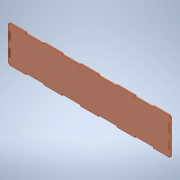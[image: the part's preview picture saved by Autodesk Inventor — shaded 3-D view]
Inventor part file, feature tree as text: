
AUTODESK INVENTOR PART (.ipt)
format: ipt  version: 2020.3 (Build 243373000, 373)  size: 240,128 bytes
history: native  units: mm
features: sketch x3, extrude x2, other x1
ambient origin geometry x8: Origin, YZ Plane, XZ Plane, XY Plane, X Axis, Y Axis, Z Axis, Center Point
bodies: Body1 (feature_tree)
feature tree (6):
  other  "Sólido1"
  extrude  "Extrusión1"  Depth=94.0mm
  sketch  "Boceto2"  dims[d2=3.0mm d3=3.0mm]
  extrude  "Extrusión2"  Depth=3.0mm
  sketch  "Boceto1"  dims[d0=3.0mm d1=94.0mm]
  sketch  "Boceto3"  dims[d4=45.0mm d5=3.0mm d6=50.0mm d7=3.0mm d8=50.0mm d9=3.0mm d10=50.0mm d11=3.0mm d12=50.0mm d13=3.0mm d14=50.0mm d15=3.0mm d16=50.0mm d17=3.0mm d18=50.0mm d19=3.0mm d20=45.0mm d21=3.0mm d22=3.0mm d23=94.0mm d41=3.0mm d42=45.0mm d43=3.0mm d44=50.0mm d45=3.0mm d46=50.0mm d58=3.0mm d59=50.0mm d60=3.0mm d61=50.0mm d62=3.0mm d63=50.0mm d64=3.0mm d65=50.0mm d66=3.0mm d67=50.0mm d68=3.0mm d69=3.0mm d70=0.0mm d71=20.0mm d72=3.0mm d73=20.0mm d75=20.0mm d76=3.0mm d77=20.0mm d78=3.0mm d79=20.0mm d80=3.0mm d81=20.0mm d82=20.0mm d83=3.0mm d84=20.0mm d85=20.0mm d86=3.0mm d87=20.0mm d88=3.0mm d89=20.0mm d90=3.0mm d91=20.0mm d92=3.0mm d93=20.0mm d94=3.0mm d95=20.0mm d96=3.0mm d97=20.0mm d98=3.0mm d99=20.0mm d100=3.0mm d101=10.0mm d102=0.0mm d103=0.5mm d104=0.872665mm]
